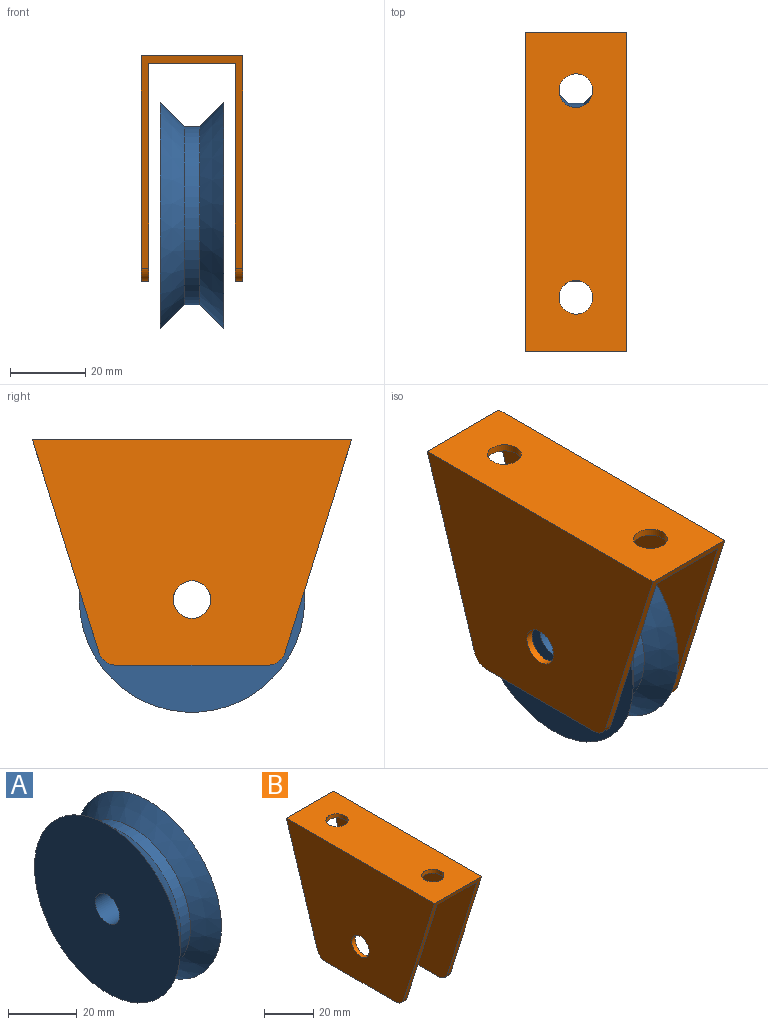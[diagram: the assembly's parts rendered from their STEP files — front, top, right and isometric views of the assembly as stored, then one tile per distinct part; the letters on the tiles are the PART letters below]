
ASSEMBLY  parts=2 mates=1
PART A: 6 faces, bbox 17x60x60 mm
  f0: plane 60x60mm, normal (-1,0,0), area 2748.9mm2, adj f4,f5
  f1: plane 60x60mm, normal (1,0,0), area 2748.9mm2, adj f2,f5
  f2: cone r=23.72mm half-angle=44deg, axis (1,0,0), area 1525.1mm2, adj f1,f3
  f3: cylinder r=23.72mm len=47.45mm, axis (-1,0,0), area 596.2mm2, adj f2,f4
  f4: cone r=30mm half-angle=44deg, axis (-1,0,0), area 1525.1mm2, adj f0,f3
  f5: cylinder r=5mm len=17mm, axis (-1,0,0), area 534.1mm2, adj f0,f1
PART B: 18 faces, bbox 27x85x60 mm
  f0: plane 85x27mm, normal (0,0,1), area 2167.8mm2, adj f1,f5,f7,f13,f16,f17
  f1: plane 56.5x27mm, normal (0,-0.95,-0.3), area 285.1mm2, adj f0,f2,f6,f7,f8,f9,f10,f13
  f2: cylinder r=5mm len=4.77mm, axis (-1,0,0), area 12.7mm2, adj f1,f3,f6,f7
  f3: plane 40x2mm, normal (0,0,-1), area 80mm2, adj f2,f4,f6,f7
  f4: cylinder r=5mm len=4.77mm, axis (-1,0,0), area 12.7mm2, adj f3,f5,f6,f7
  f5: plane 56.5x27mm, normal (0,0.95,-0.3), area 285.1mm2, adj f0,f4,f6,f7,f8,f9,f12,f13
  f6: plane 83.74x58mm, normal (1,0,0), area 3718mm2, adj f1,f2,f3,f4,f5,f8,f15
  f7: plane 85x60mm, normal (-1,0,0), area 3886.7mm2, adj f0,f1,f2,f3,f4,f5,f15
  f8: plane 83.74x23mm, normal (0,0,-1), area 1798.9mm2, adj f1,f5,f6,f9,f16,f17
  f9: plane 83.74x58mm, normal (-1,0,0), area 3718mm2, adj f1,f5,f8,f10,f11,f12,f14
  f10: cylinder r=5mm len=4.77mm, axis (-1,0,0), area 12.7mm2, adj f1,f9,f11,f13
  f11: plane 40x2mm, normal (0,0,-1), area 80mm2, adj f9,f10,f12,f13
  f12: cylinder r=5mm len=4.77mm, axis (-1,0,0), area 12.7mm2, adj f5,f9,f11,f13
  f13: plane 85x60mm, normal (1,0,0), area 3886.7mm2, adj f0,f1,f5,f10,f11,f12,f14
  f14: cylinder r=5mm len=10mm, axis (-1,0,0), area 62.8mm2, adj f9,f13
  f15: cylinder r=5mm len=10mm, axis (-1,0,0), area 62.8mm2, adj f6,f7
  f16: cylinder r=4.5mm len=9mm, axis (0,0,1), area 56.5mm2, adj f0,f8
  f17: cylinder r=4.5mm len=9mm, axis (0,0,1), area 56.5mm2, adj f0,f8
PLACE A t=(-53.08,18.25,52.62)mm
PLACE B t=(-58.08,-139.62,30.51)mm
MATE revolute A.f5 <-> B.f14  axis (-1,0,0) through (-44.58,18.25,52.62)mm
